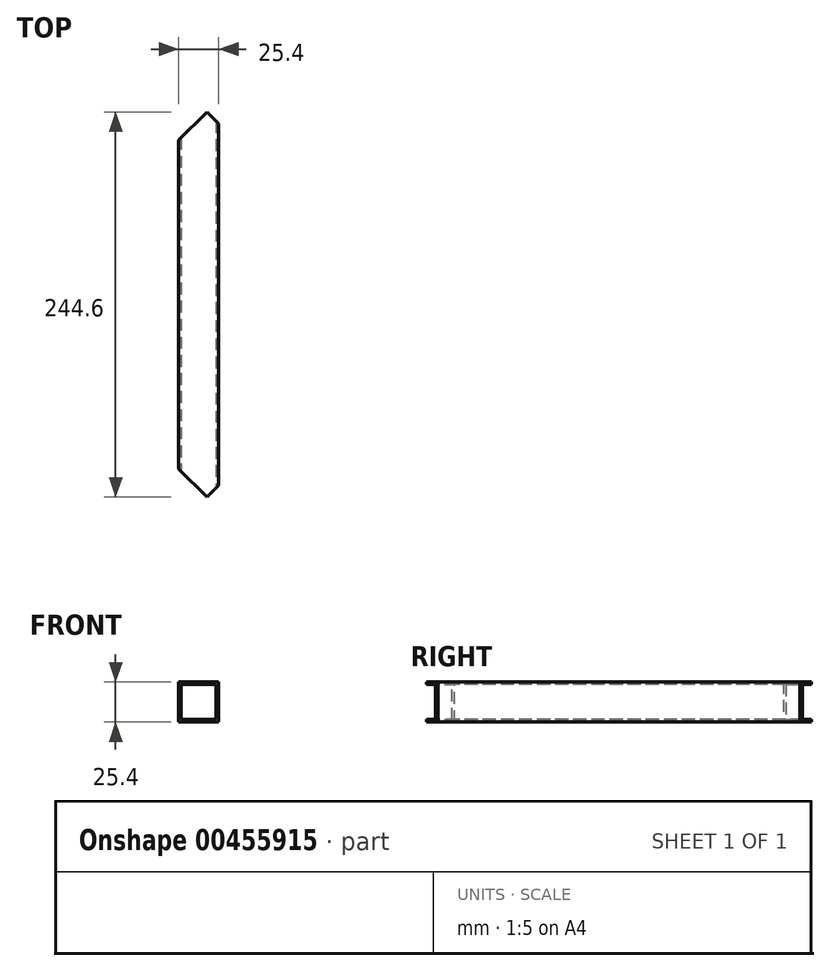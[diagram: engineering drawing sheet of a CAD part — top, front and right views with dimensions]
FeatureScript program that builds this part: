
annotation { "Feature Type Name" : "Feature", "Feature Type Description" : "" }
export const myFeature = defineFeature(function(context is Context, id is Id, definition is map)
    precondition{}
    {
        {
            var Q0;
            Q0=qCreatedBy(makeId("Top.planeOp"),FACE);
            var sketch = newSketch(context, id + "F0", { "sketchPlane" : qUnion([Q0])});
            skLineSegment(sketch, "E0.bottom", {"start": v(-12.7, 135) * mm, "end": v(12.7, 135) * mm});
            skLineSegment(sketch, "E0.top", {"start": v(-12.7, -135) * mm, "end": v(12.7, -135) * mm});
            skLineSegment(sketch, "E0.left", {"start": v(-12.7, 135) * mm, "end": v(-12.7, -135) * mm});
            skLineSegment(sketch, "E0.right", {"start": v(12.7, 135) * mm, "end": v(12.7, -135) * mm});
            skPoint(sketch, "E0.middle", {"position": v(0, 0) * mm});
            skLineSegment(sketch, "E1", {"start": v(12.7, 135) * mm, "end": v(-12.7, 109.6) * mm});
            skPoint(sketch, "E2", {"position": v(5.26, 127.56) * mm});
            skLineSegment(sketch, "E3", {"start": v(5.26, 127.56) * mm, "end": v(12.7, 120.12) * mm});
            skSolve(sketch);
        }
        {
            var Q0;
            {var subQ0=sQuery(id+"F0.wireOp",EDGE,"E3");Q0=makeQuery(id+"F0.imprint","IMPRINT",FACE,{"disambiguationData":[TD([[makeQuery(id+"F0.imprint","IMPRINT",EDGE,{"derivedFrom":subQ0}),-1.0]])]});}
            extrude(context, id + "F1", {"entities" : qUnion([Q0]), "depth" : 25.4 * mm});
        }
        {
            var Q0;
            Q0=makeQuery(id+"F1.opExtrude","SWEPT_FACE",FACE,{"disambiguationData":[OSD([sQuery(id+"F0.wireOp",EDGE,"E0.top")])]});
            shell(context, id + "F2", {"entities" : qUnion([Q0]), "thickness" : 1.59 * mm});
        }
        {
            var Q0;
            Q0=makeQuery(id+"F1.opExtrude","SWEPT_FACE",FACE,{"disambiguationData":[OSD([sQuery(id+"F0.wireOp",EDGE,"E0.top")])]});
            var sketch = newSketch(context, id + "F3", { "sketchPlane" : qUnion([Q0])});
            skLineSegment(sketch, "E4.bottom", {"start": v(-11.11, 23.81) * mm, "end": v(11.11, 23.81) * mm});
            skLineSegment(sketch, "E4.top", {"start": v(-11.11, 1.59) * mm, "end": v(11.11, 1.59) * mm});
            skLineSegment(sketch, "E4.left", {"start": v(-11.11, 23.81) * mm, "end": v(-11.11, 1.59) * mm});
            skLineSegment(sketch, "E4.right", {"start": v(11.11, 23.81) * mm, "end": v(11.11, 1.59) * mm});
            skSolve(sketch);
        }
        {
            var Q0;
            Q0=qSketchRegion(id+"F3",true);
            extrude(context, id + "F4", {"entities" : qUnion([Q0]), "operationType" : NewBodyOperationType.REMOVE, "endBound" : BoundingType.THROUGH_ALL, "oppositeDirection" : true, "depth" : 25.4 * mm});
        }
        {
            var Q0;
            Q0=makeQuery(id+"F1.opExtrude","CAP_FACE",FACE,{"disambiguationData":[OSD([sQuery(id+"F0.wireOp",EDGE,"E0.top"),sQuery(id+"F0.wireOp",EDGE,"E0.left"),sQuery(id+"F0.wireOp",EDGE,"E0.right"),sQuery(id+"F0.wireOp",EDGE,"E1"),sQuery(id+"F0.wireOp",EDGE,"E3")])],"isStart":false});
            var sketch = newSketch(context, id + "F5", { "sketchPlane" : qUnion([Q0])});
            skLineSegment(sketch, "E5", {"start": v(-12.7, -135) * mm, "end": v(12.7, -109.6) * mm});
            skPoint(sketch, "E6", {"position": v(5.26, -117.04) * mm});
            skLineSegment(sketch, "E7", {"start": v(5.26, -117.04) * mm, "end": v(-12.7, -99.08) * mm});
            skSolve(sketch);
        }
        {
            var Q0;
            {var subQ0=sQuery(id+"F5.wireOp",EDGE,"E5");Q0=makeQuery(id+"F5.imprint","IMPRINT",FACE,{"disambiguationData":[TD([[makeQuery(id+"F5.imprint","IMPRINT",EDGE,{"derivedFrom":subQ0}),-1.0]])]});}
            var Q1;
            {var subQ3=sQuery(id+"F5.wireOp",EDGE,"E7");Q1=makeQuery(id+"F5.imprint","IMPRINT",FACE,{"disambiguationData":[TD([[makeQuery(id+"F5.imprint","IMPRINT",EDGE,{"derivedFrom":subQ3}),1.0]])]});}
            extrude(context, id + "F6", {"entities" : qUnion([Q0, Q1]), "operationType" : NewBodyOperationType.REMOVE, "oppositeDirection" : true, "depth" : 25.4 * mm});
        }
    });
